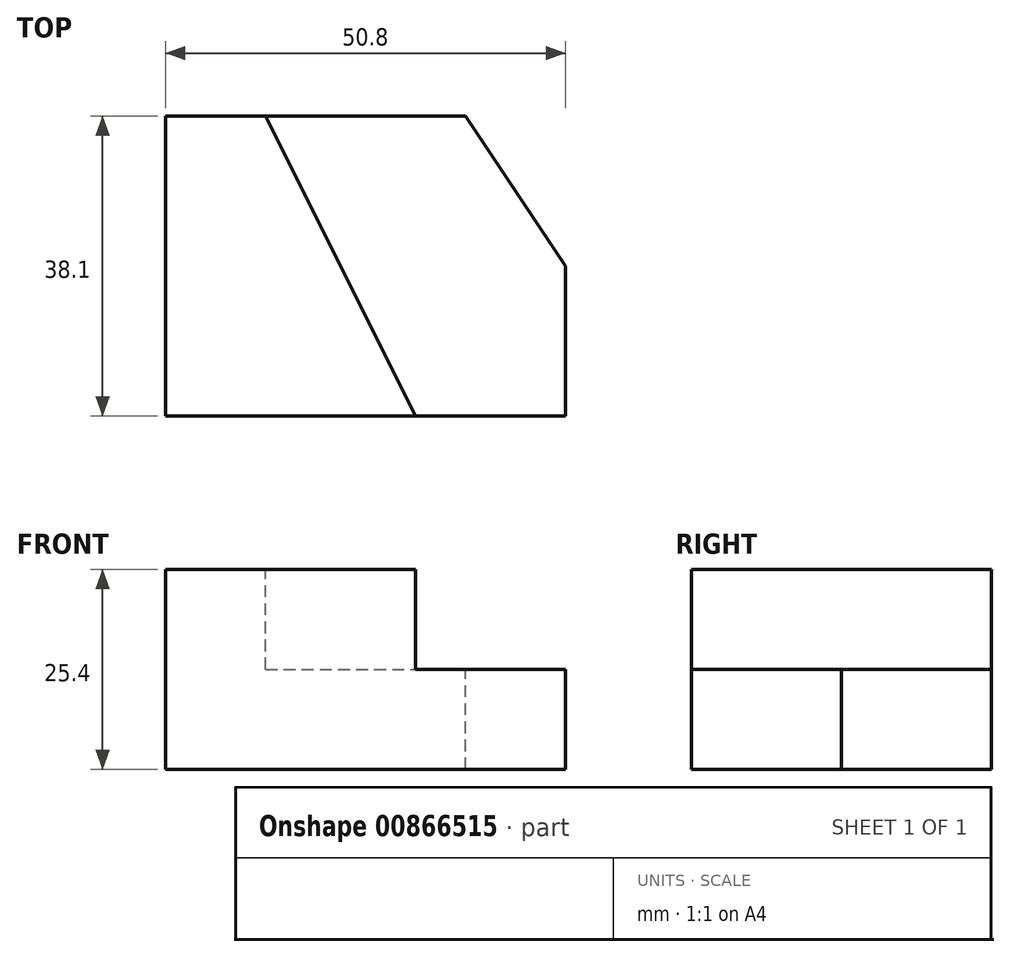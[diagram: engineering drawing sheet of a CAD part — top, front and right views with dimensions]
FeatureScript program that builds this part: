
annotation { "Feature Type Name" : "Feature", "Feature Type Description" : "" }
export const myFeature = defineFeature(function(context is Context, id is Id, definition is map)
    precondition{}
    {
        {
            var Q0;
            Q0=qCreatedBy(makeId("Top.planeOp"),FACE);
            var sketch = newSketch(context, id + "F0", { "sketchPlane" : qUnion([Q0])});
            skLineSegment(sketch, "E0.bottom", {"start": v(39.9, -21.04) * mm, "end": v(90.7, -21.04) * mm});
            skLineSegment(sketch, "E0.top", {"start": v(39.9, -59.14) * mm, "end": v(90.7, -59.14) * mm});
            skLineSegment(sketch, "E0.left", {"start": v(39.9, -21.04) * mm, "end": v(39.9, -59.14) * mm});
            skLineSegment(sketch, "E0.right", {"start": v(90.7, -21.04) * mm, "end": v(90.7, -59.14) * mm});
            skSolve(sketch);
        }
        {
            var Q0;
            Q0 = qSketchRegion(id + "F0", true);
            extrude(context, id + "F1", {"entities" : qUnion([Q0]), "depth" : 25.4 * mm, "offsetDistance" : 25.4 * mm});
        }
        {
            var Q0;
            Q0=makeQuery(id+"F1.opExtrude","CAP_FACE",FACE,{"disambiguationData":[OSD([sQuery(id+"F0.wireOp",EDGE,"E0.bottom"),sQuery(id+"F0.wireOp",EDGE,"E0.top"),sQuery(id+"F0.wireOp",EDGE,"E0.left"),sQuery(id+"F0.wireOp",EDGE,"E0.right")])],"isStart":false});
            var sketch = newSketch(context, id + "F2", { "sketchPlane" : qUnion([Q0])});
            skLineSegment(sketch, "E1", {"start": v(52.6, -21.04) * mm, "end": v(71.64, -59.14) * mm});
            skSolve(sketch);
        }
        {
            var Q0;
            {var subQ0=sQuery(id+"F2.wireOp",EDGE,"E1");Q0=makeQuery(id+"F2.imprint","IMPRINT",FACE,{"disambiguationData":[TD([[makeQuery(id+"F2.imprint","IMPRINT",EDGE,{"derivedFrom":subQ0}),1.0]])]});}
            extrude(context, id + "F3", {"entities" : qUnion([Q0]), "operationType" : NewBodyOperationType.REMOVE, "oppositeDirection" : true, "depth" : 12.7 * mm, "offsetDistance" : 25.4 * mm});
        }
        {
            var Q0;
            Q0=makeQuery(id+"F3.boolean.opBoolean","COPY",FACE,{"derivedFrom":makeQuery(id+"F3.opExtrude","CAP_FACE",FACE,{"disambiguationData":[OSD([sQuery(id+"F0.wireOp",EDGE,"E0.bottom"),sQuery(id+"F0.wireOp",EDGE,"E0.top"),sQuery(id+"F0.wireOp",EDGE,"E0.right"),sQuery(id+"F2.wireOp",EDGE,"E1")])],"isStart":false})});
            var sketch = newSketch(context, id + "F4", { "sketchPlane" : qUnion([Q0])});
            skLineSegment(sketch, "E2", {"start": v(78, -21.04) * mm, "end": v(78, -40.1) * mm});
            skLineSegment(sketch, "E3", {"start": v(90.7, -40.1) * mm, "end": v(78, -40.1) * mm});
            skLineSegment(sketch, "E4", {"start": v(78, -21.04) * mm, "end": v(90.7, -40.1) * mm});
            skSolve(sketch);
        }
        {
            var Q0;
            {var subQ0=sQuery(id+"F4.wireOp",EDGE,"E4");Q0=makeQuery(id+"F4.imprint","IMPRINT",FACE,{"disambiguationData":[TD([[makeQuery(id+"F4.imprint","IMPRINT",EDGE,{"derivedFrom":subQ0}),1.0]])]});}
            extrude(context, id + "F5", {"entities" : qUnion([Q0]), "operationType" : NewBodyOperationType.REMOVE, "oppositeDirection" : true, "depth" : 25.4 * mm, "offsetDistance" : 25.4 * mm});
        }
    });
